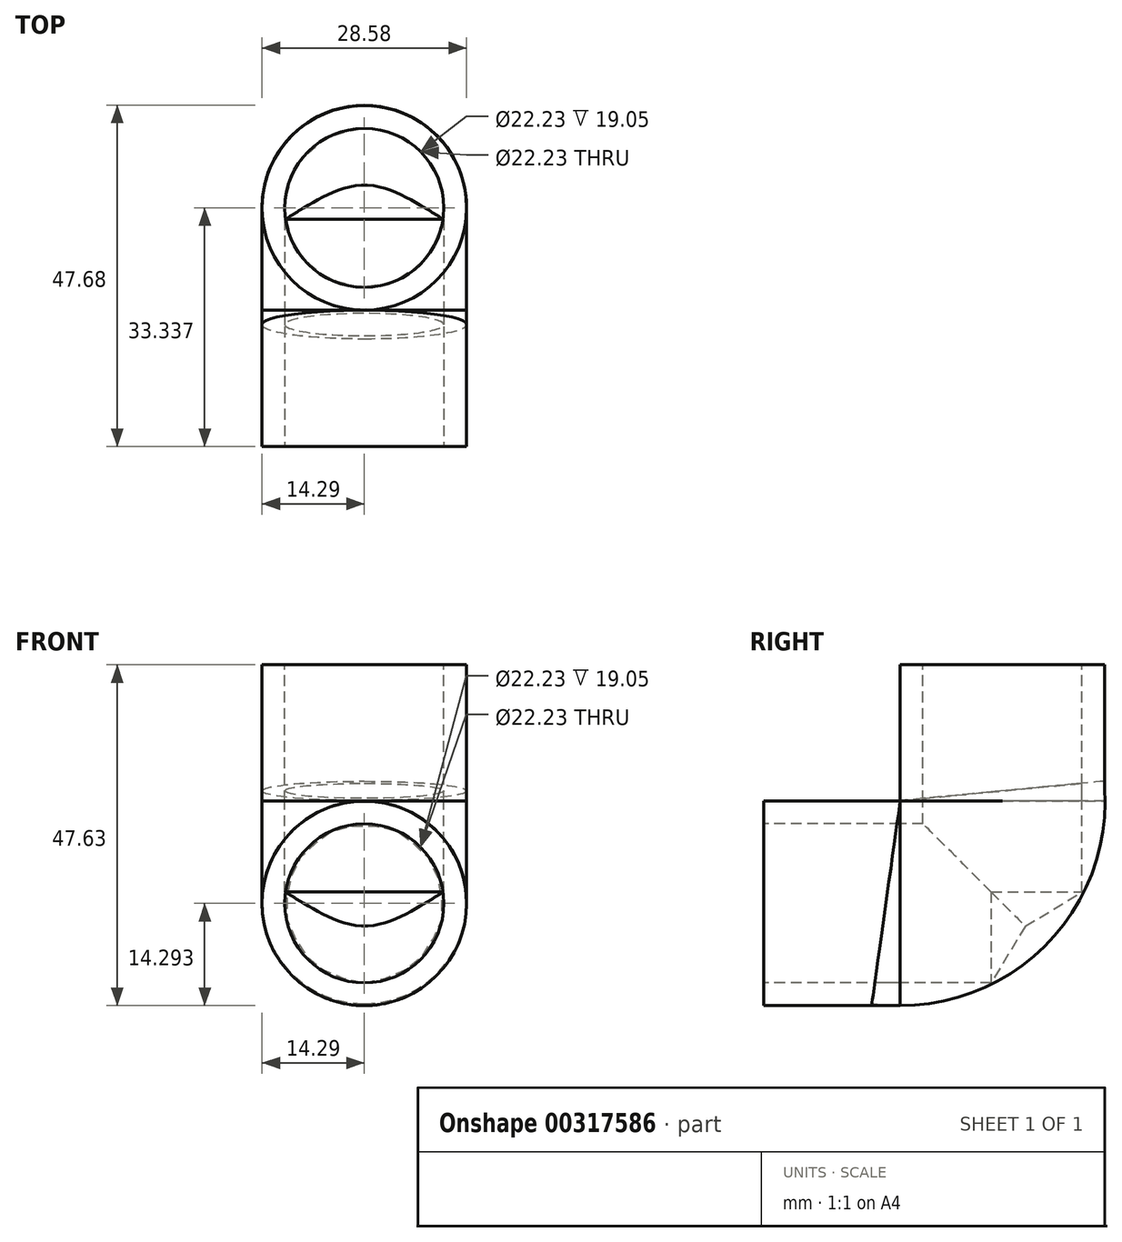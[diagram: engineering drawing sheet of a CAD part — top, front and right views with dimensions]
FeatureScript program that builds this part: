
annotation { "Feature Type Name" : "Feature", "Feature Type Description" : "" }
export const myFeature = defineFeature(function(context is Context, id is Id, definition is map)
    precondition{}
    {
        {
            var Q0;
            Q0=qCreatedBy(makeId("Top.planeOp"),FACE);
            var sketch = newSketch(context, id + "F0", { "sketchPlane" : qUnion([Q0])});
            skCircle(sketch, "E0", {"center": v(0, 33.34) * mm, "radius": 14.29 * mm});
            skSolve(sketch);
        }
        {
            var Q0;
            Q0=qCreatedBy(makeId("Front.planeOp"),FACE);
            var sketch = newSketch(context, id + "F1", { "sketchPlane" : qUnion([Q0])});
            skCircle(sketch, "E1", {"center": v(0, -33.34) * mm, "radius": 14.29 * mm});
            skSolve(sketch);
        }
        {
            var Q0;
            Q0=makeQuery(id+"F1.imprint","IMPRINT",FACE,{"disambiguationData":[TD([[makeQuery(id+"F1.imprint","IMPRINT",EDGE,{"derivedFrom":sQuery(id+"F1.wireOp",EDGE,"E1")}),1.0]])]});
            extrude(context, id + "F2", {"entities" : qUnion([Q0]), "oppositeDirection" : true, "depth" : 19.05 * mm});
        }
        {
            var Q0;
            Q0=makeQuery(id+"F0.imprint","IMPRINT",FACE,{"disambiguationData":[TD([[makeQuery(id+"F0.imprint","IMPRINT",EDGE,{"derivedFrom":sQuery(id+"F0.wireOp",EDGE,"E0")}),1.0]])]});
            extrude(context, id + "F3", {"entities" : qUnion([Q0]), "operationType" : NewBodyOperationType.ADD, "oppositeDirection" : true, "depth" : 19.05 * mm});
        }
        {
            var Q0;
            Q0=qCreatedBy(makeId("Right.planeOp"),FACE);
            var sketch = newSketch(context, id + "F4", { "sketchPlane" : qUnion([Q0])});
            skArc(sketch, "E2", {"start": v(17.12, -32.73) * mm, "mid": v(28.64, -29.01) * mm, "end": v(32.85, -17.67) * mm});
            skSolve(sketch);
        }
        {
            var Q0;
            Q0=makeQuery(id+"F2.opExtrude","CAP_FACE",FACE,{"disambiguationData":[OSD([sQuery(id+"F1.wireOp",EDGE,"E1")])],"isStart":false});
            var Q1;
            Q1=sQuery(id+"F4.wireOp",EDGE,"E2");
            sweep(context, id + "F5", {"profiles" : qUnion([Q0]), "path" : qUnion([Q1])});
        }
        {
            var Q0;
            Q0=makeQuery(id+"F3.opExtrude","CAP_FACE",FACE,{"disambiguationData":[OSD([sQuery(id+"F0.wireOp",EDGE,"E0")])],"isStart":true});
            var sketch = newSketch(context, id + "F6", { "sketchPlane" : qUnion([Q0])});
            skCircle(sketch, "E3", {"center": v(0, 33.34) * mm, "radius": 11.11 * mm});
            skSolve(sketch);
        }
        {
            var Q0;
            Q0=sQuery(id+"F6.wireOp",VERTEX,"E3.center");
            var Q1;
            Q1=makeQuery(id+"F3.opExtrude","SWEPT_BODY",BODY,{"disambiguationData":[OSD([sQuery(id+"F0.wireOp",EDGE,"E0")])]});
            var Q2;
            Q2=makeQuery(id+"F5.opSweep","SWEPT_BODY",BODY,{"disambiguationData":[OSD([sQuery(id+"F1.wireOp",EDGE,"E1"),sQuery(id+"F4.wireOp",EDGE,"E2")])]});
            hole(context, id + "F7", {"style" : HoleStyle.SIMPLE, "endStyle" : HoleEndStyle.BLIND, "holeDiameter" : 22.22 * mm, "holeDepth" : 31.75 * mm, "tappedDepth" : 12.7 * mm, "tapClearance" : 3, "locations" : qUnion([Q0]), "scope" : qUnion([Q1, Q2])});
        }
        {
            var Q0;
            Q0=makeQuery(id+"F2.opExtrude","CAP_FACE",FACE,{"disambiguationData":[OSD([sQuery(id+"F1.wireOp",EDGE,"E1")])],"isStart":true});
            var sketch = newSketch(context, id + "F8", { "sketchPlane" : qUnion([Q0])});
            skCircle(sketch, "E4", {"center": v(0, -33.34) * mm, "radius": 11.11 * mm});
            skSolve(sketch);
        }
        {
            var Q0;
            Q0=sQuery(id+"F8.wireOp",VERTEX,"E4.center");
            var Q1;
            Q1=makeQuery(id+"F2.opExtrude","SWEPT_BODY",BODY,{"disambiguationData":[OSD([sQuery(id+"F1.wireOp",EDGE,"E1")])]});
            var Q2;
            Q2=makeQuery(id+"F5.opSweep","SWEPT_BODY",BODY,{"disambiguationData":[OSD([sQuery(id+"F1.wireOp",EDGE,"E1"),sQuery(id+"F4.wireOp",EDGE,"E2")])]});
            hole(context, id + "F9", {"style" : HoleStyle.SIMPLE, "endStyle" : HoleEndStyle.BLIND, "holeDiameter" : 22.22 * mm, "holeDepth" : 31.75 * mm, "tappedDepth" : 12.7 * mm, "tapClearance" : 3, "locations" : qUnion([Q0]), "scope" : qUnion([Q1, Q2])});
        }
    });
